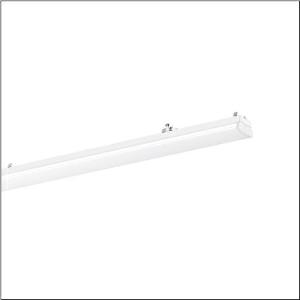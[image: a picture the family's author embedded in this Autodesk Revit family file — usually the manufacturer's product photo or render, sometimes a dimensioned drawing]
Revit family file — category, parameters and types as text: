
# Revit family: licross_r__11_recessed_opal_ho_51tl1ddv4m1m_211a
name_source: partatom
category: Lighting Fixtures
units: mm (PartAtom-declared; Revit-internal decimal feet)

## family parameters
Cut with Voids When Loaded = No
Host = Face
Light Source = No
Part Type = Normal
Room Calculation Point = No
Round Connector Dimension = Use Diameter
Shared = No

## types (1)
- --- (1 x LED, 26350 lm, 150.5 W, 4000K)
    Apparent Load = 150 VA
    CIE Flux Codes = 44 73 91 87 100
    Color Rendering = 80
    Color Temperature = 4000K
    Default Elevation = 1800 mm
    Description = Licross® 11 recessed opal HO, luminaire insert, of sheet steel, coil coated, white, length: 2.250mm, width: 76mm, height: 87mm, LED rated luminous flux: 26.350lm, light colour: 840, control gear: DALI 2, with plug, 5-pole, with phase selection, mains connection: 220..240V, AC, 50/60Hz, rated input power: 151W, halogen-free wiring, primary optical cover: cover, of PMMA, light emission: direct with ceiling illumination distribution, primary light characteristic: symmetric, protection rating (complete): IP40, insulation class (complete): insulation class I (protective earthing), certification: CE, ENEC, VDE, UKCA, protection symbol: D if used in an environment without relevant dust loads with corresponding accessories, impact resistance: IK06, permissible ambient temperature for indoor applications: -40..+35°C, corresponds to IFS (International Featured Standards) requirements for safety and quality in the food industry, reducing of maximum allowable ambient temperature of 5°C with ceiling mounting, LABS conformity tested according to VDMA 24364:2018-05, packaging unit: 1 piece
    Height = 83 mm
    Lamp = 1 x LED
    Lamp Light Flux = 26350 lm
    Lamp Power = 150.5 W
    Lamp count = 1
    Length = 2250 mm
    Luminous efficacy = 175 lm/W
    Manufacturer = Siteco
    ModVariant = No
    Model = 51TL1DDV4M1M
    Mounting Place = Ceiling
    Mounting Type = Pendant
    Number of Poles = 1
    OnlyDefault = Yes
    Power Factor = 1
    Product Name = Licross® 11 recessed opal HO
    Product group = luminaire insert
    ProductGroupID = 901
    Protection Class = Protection class I
    Protection Degree = IP 40
    RLX_Detail_Level = 1
    RLX_Emergency_Light_Flux = 0 lm
    RLX_Emergency_Type = 0
    RLX_Emergency_Type_DB = No
    RlxData = <blob elided: 27233 chars, md5=59f0556a>
    Socket = socket
    Standby Power = 0 W
    System Light Flux = 26350 lm
    System Power = 150 W
    Type Comments = factory setting: luminous flux: 100 % | dim-lin: 254 | 690 mA
    Type Image = l_1313666.jpg
    URL = http://relux.com
    VarID = @adj_045407
    Voltage = 0 V
    Weight = 0.00 kg
    Width = 76 mm

## geometry (parser evidence)
native form markers: Blend x4, Sweep x10
no freeform markers — native parametric forms only
